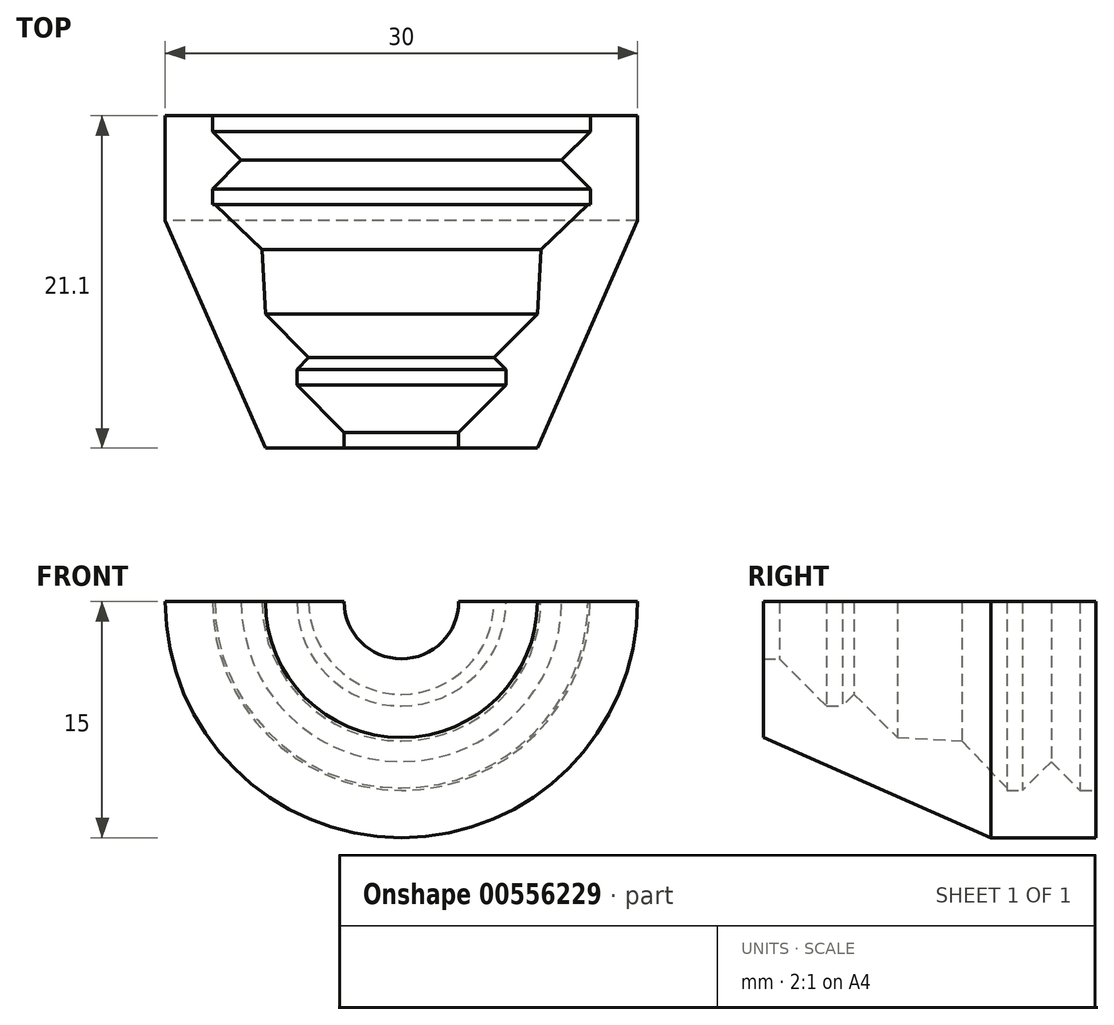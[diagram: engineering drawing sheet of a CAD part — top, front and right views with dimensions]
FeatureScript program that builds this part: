
annotation { "Feature Type Name" : "Feature", "Feature Type Description" : "" }
export const myFeature = defineFeature(function(context is Context, id is Id, definition is map)
    precondition{}
    {
        {
            var Q0;
            Q0=qCreatedBy(makeId("Top.planeOp"),FACE);
            var sketch = newSketch(context, id + "F0", { "sketchPlane" : qUnion([Q0])});
            skLineSegment(sketch, "E0", {"start": v(-15, 10.65) * mm, "end": v(-9, 10.65) * mm});
            skLineSegment(sketch, "E1", {"start": v(-9, 10.65) * mm, "end": v(-9, 6.65) * mm});
            skLineSegment(sketch, "E2", {"start": v(-9, 6.65) * mm, "end": v(-12, 6.65) * mm});
            skLineSegment(sketch, "E3", {"start": v(-12, 6.65) * mm, "end": v(-12, 5.65) * mm});
            skLineSegment(sketch, "E4", {"start": v(-12, 5.65) * mm, "end": v(-9, 5.65) * mm});
            skLineSegment(sketch, "E5", {"start": v(-9, 2) * mm, "end": v(-12, 2) * mm});
            skLineSegment(sketch, "E6", {"start": v(-12, 2) * mm, "end": v(-12, 1) * mm});
            skLineSegment(sketch, "E7", {"start": v(-12, 1) * mm, "end": v(-9, 1) * mm});
            skLineSegment(sketch, "E8", {"start": v(-3.64, -9.45) * mm, "end": v(-6.64, -9.45) * mm});
            skLineSegment(sketch, "E9", {"start": v(-6.64, -9.45) * mm, "end": v(-6.64, -10.45) * mm});
            skLineSegment(sketch, "E10", {"start": v(-6.64, -10.45) * mm, "end": v(-3.64, -10.45) * mm});
            skLineSegment(sketch, "E11", {"start": v(-3.64, -10.45) * mm, "end": v(-3.64, -14.45) * mm});
            skLineSegment(sketch, "E12", {"start": v(-3.64, -14.45) * mm, "end": v(-8.64, -14.45) * mm});
            skLineSegment(sketch, "E13", {"start": v(0, 15) * mm, "end": v(0, -15) * mm});
            skLineSegment(sketch, "E14", {"start": v(-9, 2) * mm, "end": v(-9, 5.65) * mm});
            skLineSegment(sketch, "E15", {"start": v(-15, 10.65) * mm, "end": v(-15, 0) * mm});
            skLineSegment(sketch, "E16", {"start": v(-15, 0) * mm, "end": v(-8.64, -14.45) * mm});
            skLineSegment(sketch, "E17", {"start": v(-3.64, -9.45) * mm, "end": v(-3.64, -5.95) * mm});
            skLineSegment(sketch, "E18", {"start": v(-3.64, -5.95) * mm, "end": v(-8.64, -5.95) * mm});
            skLineSegment(sketch, "E19", {"start": v(-9, 1) * mm, "end": v(-8.64, -5.95) * mm});
            skSolve(sketch);
        }
        {
            var Q0;
            Q0=makeQuery(id+"F0.imprint","IMPRINT",FACE,{"disambiguationData":[TD([[makeQuery(id+"F0.imprint","IMPRINT",EDGE,{"derivedFrom":sQuery(id+"F0.wireOp",EDGE,"E0")}),-1.0]])]});
            var Q1;
            Q1=sQuery(id+"F0.wireOp",EDGE,"E13");
            revolve(context, id + "F1", {"entities" : qUnion([Q0]), "axis" : qUnion([Q1]), "revolveType" : RevolveType.ONE_DIRECTION, "angle" : 180 * degree});
        }
        {
            var Q0;
            Q0=makeQuery(id+"F1.opRevolve","SWEPT_EDGE",EDGE,{"disambiguationData":[OSD([sQuery(id+"F0.wireOp",EDGE,"E7"),sQuery(id+"F0.wireOp",EDGE,"E19")])]});
            var Q1;
            Q1=makeQuery(id+"F1.opRevolve","SWEPT_EDGE",EDGE,{"disambiguationData":[OSD([sQuery(id+"F0.wireOp",EDGE,"E5"),sQuery(id+"F0.wireOp",EDGE,"E14")])]});
            var Q2;
            Q2=makeQuery(id+"F1.opRevolve","SWEPT_EDGE",EDGE,{"disambiguationData":[OSD([sQuery(id+"F0.wireOp",EDGE,"E4"),sQuery(id+"F0.wireOp",EDGE,"E14")])]});
            var Q3;
            Q3=makeQuery(id+"F1.opRevolve","SWEPT_EDGE",EDGE,{"disambiguationData":[OSD([sQuery(id+"F0.wireOp",EDGE,"E1"),sQuery(id+"F0.wireOp",EDGE,"E2")])]});
            var Q4;
            Q4=makeQuery(id+"F1.opRevolve","SWEPT_EDGE",EDGE,{"disambiguationData":[OSD([sQuery(id+"F0.wireOp",EDGE,"E8"),sQuery(id+"F0.wireOp",EDGE,"E17")])]});
            var Q5;
            Q5=makeQuery(id+"F1.opRevolve","SWEPT_EDGE",EDGE,{"disambiguationData":[OSD([sQuery(id+"F0.wireOp",EDGE,"E10"),sQuery(id+"F0.wireOp",EDGE,"E11")])]});
            chamfer(context, id + "F2", {"entities" : qUnion([Q0, Q1, Q2, Q3, Q4, Q5]), "width" : 3 * mm, "tangentPropagation" : true});
        }
        {
            var Q0;
            Q0=makeQuery(id+"F1.opRevolve","SWEPT_EDGE",EDGE,{"disambiguationData":[OSD([sQuery(id+"F0.wireOp",EDGE,"E0"),sQuery(id+"F0.wireOp",EDGE,"E15")])]});
            chamfer(context, id + "F3", {"entities" : qUnion([Q0]), "width" : 4 * mm, "tangentPropagation" : true});
        }
        {
            var Q0;
            Q0=makeQuery(id+"F1.opRevolve","CAP_FACE",FACE,{"disambiguationData":[OSD([sQuery(id+"F0.wireOp",EDGE,"E0"),sQuery(id+"F0.wireOp",EDGE,"E1"),sQuery(id+"F0.wireOp",EDGE,"E2"),sQuery(id+"F0.wireOp",EDGE,"E3"),sQuery(id+"F0.wireOp",EDGE,"E4"),sQuery(id+"F0.wireOp",EDGE,"E5"),sQuery(id+"F0.wireOp",EDGE,"E6"),sQuery(id+"F0.wireOp",EDGE,"E7"),sQuery(id+"F0.wireOp",EDGE,"E8"),sQuery(id+"F0.wireOp",EDGE,"E9"),sQuery(id+"F0.wireOp",EDGE,"E10"),sQuery(id+"F0.wireOp",EDGE,"E11"),sQuery(id+"F0.wireOp",EDGE,"E12"),sQuery(id+"F0.wireOp",EDGE,"E14"),sQuery(id+"F0.wireOp",EDGE,"E15"),sQuery(id+"F0.wireOp",EDGE,"E16"),sQuery(id+"F0.wireOp",EDGE,"E17"),sQuery(id+"F0.wireOp",EDGE,"E18"),sQuery(id+"F0.wireOp",EDGE,"E19")])],"isStart":true});
            var sketch = newSketch(context, id + "F4", { "sketchPlane" : qUnion([Q0])});
            skLineSegment(sketch, "E20.bottom", {"start": v(-15, 10.65) * mm, "end": v(15, 10.65) * mm});
            skLineSegment(sketch, "E20.top", {"start": v(-15, 6.65) * mm, "end": v(15, 6.65) * mm});
            skLineSegment(sketch, "E20.left", {"start": v(-15, 10.65) * mm, "end": v(-15, 6.65) * mm});
            skLineSegment(sketch, "E20.right", {"start": v(15, 10.65) * mm, "end": v(15, 6.65) * mm});
            skSolve(sketch);
        }
        {
            var Q0;
            {var subQ4=sQuery(id+"F4.wireOp",EDGE,"E20.left");Q0=makeQuery(id+"F4.imprint","IMPRINT",FACE,{"disambiguationData":[TD([[makeQuery(id+"F4.imprint","IMPRINT",EDGE,{"derivedFrom":subQ4}),1.0]])]});}
            var Q1;
            {var subQ0=sQuery(id+"F0.wireOp",EDGE,"E1");var subQ1=makeQuery(id+"F1.opRevolve","CAP_EDGE",EDGE,{"disambiguationData":[OSD([subQ0])],"isStart":true});Q1=makeQuery(id+"F4.imprint","IMPRINT",FACE,{"disambiguationData":[TD([[makeQuery(id+"F4.imprint","IMPRINT",EDGE,{"derivedFrom":subQ1}),-1.0]])]});}
            var Q2;
            {var subQ4=sQuery(id+"F4.wireOp",EDGE,"E20.right");Q2=makeQuery(id+"F4.imprint","IMPRINT",FACE,{"disambiguationData":[TD([[makeQuery(id+"F4.imprint","IMPRINT",EDGE,{"derivedFrom":subQ4}),-1.0]])]});}
            extrude(context, id + "F5", {"entities" : qUnion([Q0, Q1, Q2]), "operationType" : NewBodyOperationType.REMOVE, "endBound" : BoundingType.THROUGH_ALL, "oppositeDirection" : true, "depth" : 25 * mm, "offsetDistance" : 25 * mm});
        }
        {
            var Q0;
            Q0=makeQuery(id+"F1.opRevolve","SWEPT_EDGE",EDGE,{"disambiguationData":[OSD([sQuery(id+"F0.wireOp",EDGE,"E17"),sQuery(id+"F0.wireOp",EDGE,"E18")])]});
            chamfer(context, id + "F6", {"entities" : qUnion([Q0]), "width" : 5 * mm, "tangentPropagation" : true});
        }
    });
